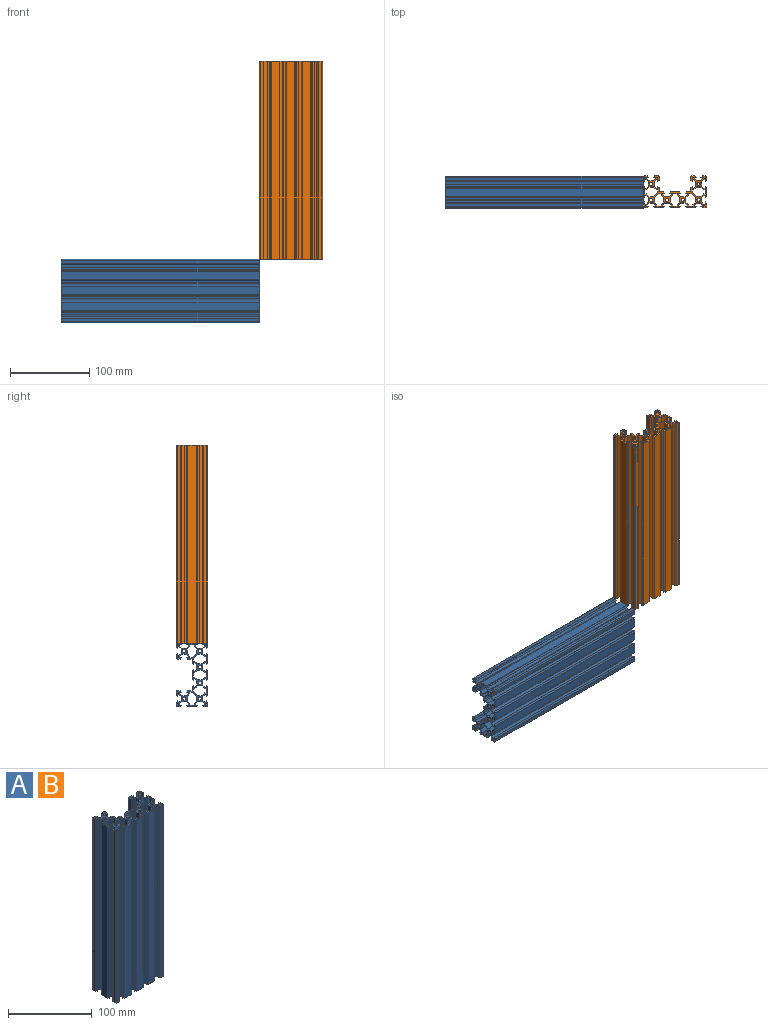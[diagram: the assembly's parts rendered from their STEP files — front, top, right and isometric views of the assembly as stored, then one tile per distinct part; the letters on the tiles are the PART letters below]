
ASSEMBLY  parts=2 mates=1
PART A: 346 faces, bbox 80x40x250 mm
  f0: cylinder r=2.1mm len=250mm, axis (0,0,-1), area 3298.7mm2, adj f6,f7
  f1: cylinder r=2.1mm len=250mm, axis (0,0,-1), area 3298.7mm2, adj f6,f7
  f2: cylinder r=2.1mm len=250mm, axis (0,0,-1), area 3298.7mm2, adj f6,f7
  f3: cylinder r=2.1mm len=250mm, axis (0,0,-1), area 3298.7mm2, adj f6,f7
  f4: cylinder r=2.1mm len=250mm, axis (0,0,-1), area 3298.7mm2, adj f6,f7
  f5: cylinder r=2.1mm len=250mm, axis (0,0,-1), area 3298.7mm2, adj f6,f7
  f6: plane 80x40mm, normal (0,0,1), area 810.2mm2, adj f0,f1,f2,f3,f4,f5,f8,f9
  f7: plane 80x40mm, normal (0,0,-1), area 810.2mm2, adj f0,f1,f2,f3,f4,f5,f8,f9
  f8: plane 250x0.11mm, normal (0.68,0.73,0), area 36.6mm2, adj f6,f7,f9,f259
  f9: plane 250x2.73mm, normal (0,1,0), area 682.1mm2, adj f6,f7,f8,f10
  f10: plane 250x2.66mm, normal (0.71,0.71,0), area 940.4mm2, adj f6,f7,f9,f11
  f11: plane 250x1.64mm, normal (1,0,0), area 410.5mm2, adj f6,f7,f10,f12
  f12: plane 250x2.61mm, normal (0,-1,0), area 653.3mm2, adj f6,f7,f11,f13
  f13: plane 250x0.11mm, normal (1,0,0), area 27.9mm2, adj f6,f7,f12,f14
  f14: plane 250x1.46mm, normal (0.71,0.71,0), area 515.7mm2, adj f6,f7,f13,f15
  f15: cylinder r=0.79mm len=250mm, axis (0,0,-1), area 155.1mm2, adj f6,f7,f14,f16
  f16: plane 250x3.6mm, normal (0,1,0), area 899mm2, adj f6,f7,f15,f17
  f17: cylinder r=1.5mm len=250mm, axis (0,0,-1), area 590.6mm2, adj f6,f7,f16,f18
  f18: plane 250x3.61mm, normal (-1,0,0), area 901.5mm2, adj f6,f7,f17,f19
  f19: cylinder r=0.79mm len=250mm, axis (0,0,-1), area 155.1mm2, adj f6,f7,f18,f20
  f20: plane 250x1.46mm, normal (-0.71,-0.71,0), area 515.7mm2, adj f6,f7,f19,f21
  f21: plane 250x0.11mm, normal (0,-1,0), area 27.5mm2, adj f6,f7,f20,f22
  f22: plane 250x2.61mm, normal (1,0,0), area 653.3mm2, adj f6,f7,f21,f23
  f23: plane 250x1.64mm, normal (0,-1,0), area 410mm2, adj f6,f7,f22,f24
  f24: plane 250x2.66mm, normal (-0.71,-0.71,0), area 940.3mm2, adj f6,f7,f23,f25
  f25: plane 250x2.74mm, normal (-1,0,0), area 684.6mm2, adj f6,f7,f24,f26
  f26: plane 250x0.1mm, normal (-0.66,-0.75,0), area 33.6mm2, adj f6,f7,f25,f27
  f27: plane 250x0.11mm, normal (-0.75,0.67,0), area 37.9mm2, adj f6,f7,f26,f28
  f28: plane 250x2.74mm, normal (-1,0,0), area 684.6mm2, adj f6,f7,f27,f29
  f29: plane 250x2.66mm, normal (-0.71,0.71,0), area 939.5mm2, adj f6,f7,f28,f30
  f30: plane 250x1.64mm, normal (0,1,0), area 410mm2, adj f6,f7,f29,f31
  f31: plane 250x2.61mm, normal (1,0,0), area 653.3mm2, adj f6,f7,f30,f32
  f32: plane 250x0.11mm, normal (0,1,0), area 27.5mm2, adj f6,f7,f31,f33
  f33: plane 250x1.46mm, normal (-0.71,0.71,0), area 514.7mm2, adj f6,f7,f32,f34
  f34: cylinder r=0.8mm len=250mm, axis (0,0,-1), area 157.1mm2, adj f6,f7,f33,f35
  f35: plane 250x10.19mm, normal (-1,0,0), area 2547.3mm2, adj f6,f7,f34,f36
  f36: cylinder r=0.8mm len=250mm, axis (0,0,-1), area 157.1mm2, adj f6,f7,f35,f37
  f37: plane 250x1.46mm, normal (-0.71,-0.71,0), area 514.7mm2, adj f6,f7,f36,f38
  f38: plane 250x0.11mm, normal (0,-1,0), area 27.5mm2, adj f6,f7,f37,f39
  f39: plane 250x2.61mm, normal (1,0,0), area 653.3mm2, adj f6,f7,f38,f40
  f40: plane 250x1.64mm, normal (0,-1,0), area 410mm2, adj f6,f7,f39,f41
  f41: plane 250x2.67mm, normal (-0.71,-0.71,0), area 941.6mm2, adj f6,f7,f40,f42
  f42: plane 250x2.74mm, normal (-1,0,0), area 684.6mm2, adj f6,f7,f41,f43
  f43: plane 250x0.09mm, normal (-0.71,-0.71,0), area 33.5mm2, adj f6,f7,f42,f44
  f44: plane 250x0.09mm, normal (-0.71,0.71,0), area 33.5mm2, adj f6,f7,f43,f45
  f45: plane 250x2.74mm, normal (-1,0,0), area 684.6mm2, adj f6,f7,f44,f46
  f46: plane 250x2.66mm, normal (-0.71,0.71,0), area 940.3mm2, adj f6,f7,f45,f47
  f47: plane 250x1.64mm, normal (0,1,0), area 410mm2, adj f6,f7,f46,f48
  f48: plane 250x2.61mm, normal (1,0,0), area 653.3mm2, adj f6,f7,f47,f49
  f49: plane 250x0.11mm, normal (0,1,0), area 27.5mm2, adj f6,f7,f48,f50
  f50: plane 250x1.46mm, normal (-0.71,0.71,0), area 515.7mm2, adj f6,f7,f49,f51
  f51: cylinder r=0.79mm len=250mm, axis (0,0,-1), area 155.1mm2, adj f6,f7,f50,f52
  f52: plane 250x3.59mm, normal (-1,0,0), area 898.2mm2, adj f6,f7,f51,f53
  f53: cylinder r=1.5mm len=250mm, axis (0,0,-1), area 589mm2, adj f6,f7,f52,f54
  f54: plane 250x3.59mm, normal (0,-1,0), area 898.2mm2, adj f6,f7,f53,f55
  f55: cylinder r=0.79mm len=250mm, axis (0,0,-1), area 158.8mm2, adj f6,f7,f54,f56
  f56: plane 250x1.46mm, normal (0.71,-0.71,0), area 515.7mm2, adj f6,f7,f55,f57
  f57: plane 250x0.11mm, normal (1,0,0), area 27.5mm2, adj f6,f7,f56,f58
  f58: plane 250x2.61mm, normal (0,1,0), area 653.3mm2, adj f6,f7,f57,f59
  f59: plane 250x1.64mm, normal (1,0,0), area 409.7mm2, adj f6,f7,f58,f60
  f60: plane 250x2.66mm, normal (0.71,-0.71,0), area 940.2mm2, adj f6,f7,f59,f61
  f61: plane 250x2.74mm, normal (0,-1,0), area 685.1mm2, adj f6,f7,f60,f62
  f62: plane 250x0.1mm, normal (0.75,-0.66,0), area 33.4mm2, adj f6,f7,f61,f63
  f63: plane 250x0.1mm, normal (-0.75,-0.66,0), area 33.4mm2, adj f6,f7,f62,f64
  f64: plane 250x2.74mm, normal (0,-1,0), area 685.1mm2, adj f6,f7,f63,f65
  f65: plane 250x2.67mm, normal (-0.71,-0.71,0), area 942.7mm2, adj f6,f7,f64,f66
  f66: plane 250x1.64mm, normal (-1,0,0), area 409.8mm2, adj f6,f7,f65,f67
  f67: plane 250x2.61mm, normal (0,1,0), area 653.3mm2, adj f6,f7,f66,f68
  f68: plane 250x0.11mm, normal (-1,0,0), area 27.5mm2, adj f6,f7,f67,f69
  f69: plane 250x1.46mm, normal (-0.71,-0.71,0), area 514.7mm2, adj f6,f7,f68,f70
  f70: cylinder r=0.8mm len=250mm, axis (0,0,-1), area 157.1mm2, adj f6,f7,f69,f71
  f71: plane 250x10.18mm, normal (0,-1,0), area 2544.3mm2, adj f6,f7,f70,f72
  f72: cylinder r=0.8mm len=250mm, axis (0,0,-1), area 157.1mm2, adj f6,f7,f71,f73
  f73: plane 250x1.46mm, normal (0.71,-0.71,0), area 514.7mm2, adj f6,f7,f72,f74
  f74: plane 250x0.11mm, normal (1,0,0), area 27.5mm2, adj f6,f7,f73,f75
  f75: plane 250x2.61mm, normal (0,1,0), area 653.3mm2, adj f6,f7,f74,f76
  f76: plane 250x1.64mm, normal (1,0,0), area 409.5mm2, adj f6,f7,f75,f77
  f77: plane 250x2.67mm, normal (0.71,-0.71,0), area 942.8mm2, adj f6,f7,f76,f78
  f78: plane 250x2.74mm, normal (0,-1,0), area 685mm2, adj f6,f7,f77,f79
  f79: plane 250x0.1mm, normal (0.71,-0.71,0), area 35.4mm2, adj f6,f7,f78,f80
  f80: plane 250x0.1mm, normal (-0.71,-0.71,0), area 35.3mm2, adj f6,f7,f79,f81
  f81: plane 250x2.74mm, normal (0,-1,0), area 684.6mm2, adj f6,f7,f80,f82
  f82: plane 250x2.67mm, normal (-0.71,-0.71,0), area 942.8mm2, adj f6,f7,f81,f83
  f83: plane 250x1.63mm, normal (-1,0.02,0), area 407.8mm2, adj f6,f7,f82,f84
  f84: plane 250x2.61mm, normal (0,1,0), area 653.3mm2, adj f6,f7,f83,f85
  f85: plane 250x0.11mm, normal (-1,0,0), area 27.5mm2, adj f6,f7,f84,f86
  f86: plane 250x1.46mm, normal (-0.71,-0.71,0), area 514.7mm2, adj f6,f7,f85,f87
  f87: cylinder r=0.8mm len=250mm, axis (0,0,-1), area 157.1mm2, adj f6,f7,f86,f88
  f88: plane 250x10.21mm, normal (0,-1,0), area 2551.6mm2, adj f6,f7,f87,f89
  f89: cylinder r=0.8mm len=250mm, axis (0,0,-1), area 157.1mm2, adj f6,f7,f88,f90
  f90: plane 250x1.46mm, normal (0.71,-0.71,0), area 514.7mm2, adj f6,f7,f89,f91
  f91: plane 250x0.11mm, normal (1,0,0), area 27.5mm2, adj f6,f7,f90,f92
  f92: plane 250x2.61mm, normal (0,1,0), area 653.3mm2, adj f6,f7,f91,f93
  f93: plane 250x1.63mm, normal (1,0.02,0), area 407.8mm2, adj f6,f7,f92,f94
  f94: plane 250x2.67mm, normal (0.71,-0.71,0), area 942.8mm2, adj f6,f7,f93,f95
  f95: plane 250x2.74mm, normal (0,-1,0), area 684.6mm2, adj f6,f7,f94,f96
  f96: plane 250x0.1mm, normal (0.71,-0.71,0), area 35.3mm2, adj f6,f7,f95,f97
  f97: plane 250x0.1mm, normal (-0.71,-0.71,0), area 35.4mm2, adj f6,f7,f96,f98
  f98: plane 250x2.74mm, normal (0,-1,0), area 685mm2, adj f6,f7,f97,f99
  f99: plane 250x2.67mm, normal (-0.71,-0.71,0), area 942.8mm2, adj f6,f7,f98,f100
  f100: plane 250x1.64mm, normal (-1,0,0), area 409.5mm2, adj f6,f7,f99,f101
  f101: plane 250x2.61mm, normal (0,1,0), area 653.3mm2, adj f6,f7,f100,f102
  f102: plane 250x0.11mm, normal (-1,0,0), area 27.5mm2, adj f6,f7,f101,f103
  f103: plane 250x1.46mm, normal (-0.71,-0.71,0), area 514.7mm2, adj f6,f7,f102,f104
  f104: cylinder r=0.8mm len=250mm, axis (0,0,-1), area 157.1mm2, adj f6,f7,f103,f105
  f105: plane 250x10.18mm, normal (0,-1,0), area 2544.3mm2, adj f6,f7,f104,f106
  f106: cylinder r=0.8mm len=250mm, axis (0,0,-1), area 157.1mm2, adj f6,f7,f105,f107
  f107: plane 250x1.46mm, normal (0.71,-0.71,0), area 514.7mm2, adj f6,f7,f106,f108
  f108: plane 250x0.11mm, normal (1,0,0), area 27.5mm2, adj f6,f7,f107,f109
  f109: plane 250x2.61mm, normal (0,1,0), area 653.3mm2, adj f6,f7,f108,f110
  f110: plane 250x1.64mm, normal (1,0,0), area 409.8mm2, adj f6,f7,f109,f111
  f111: plane 250x2.67mm, normal (0.71,-0.71,0), area 942.7mm2, adj f6,f7,f110,f112
  f112: plane 250x2.74mm, normal (0,-1,0), area 685.1mm2, adj f6,f7,f111,f113
  f113: plane 250x0.1mm, normal (0.75,-0.66,0), area 33.4mm2, adj f6,f7,f112,f114
  f114: plane 250x0.1mm, normal (-0.75,-0.66,0), area 33.4mm2, adj f6,f7,f113,f115
  f115: plane 250x2.74mm, normal (0,-1,0), area 685.1mm2, adj f6,f7,f114,f116
  f116: plane 250x2.66mm, normal (-0.71,-0.71,0), area 940.2mm2, adj f6,f7,f115,f117
  f117: plane 250x1.64mm, normal (-1,0,0), area 409.7mm2, adj f6,f7,f116,f118
  f118: plane 250x2.61mm, normal (0,1,0), area 653.3mm2, adj f6,f7,f117,f119
  f119: plane 250x0.11mm, normal (-1,0,0), area 27.5mm2, adj f6,f7,f118,f120
  f120: plane 250x1.46mm, normal (-0.71,-0.71,0), area 515.7mm2, adj f6,f7,f119,f121
  f121: cylinder r=0.79mm len=250mm, axis (0,0,-1), area 158.8mm2, adj f6,f7,f120,f122
  f122: plane 250x3.59mm, normal (0,-1,0), area 898.2mm2, adj f6,f7,f121,f123
  f123: cylinder r=1.5mm len=250mm, axis (0,0,-1), area 589mm2, adj f6,f7,f122,f124
  f124: plane 250x3.59mm, normal (1,0,0), area 898.2mm2, adj f6,f7,f123,f125
  f125: cylinder r=0.79mm len=250mm, axis (0,0,-1), area 155.1mm2, adj f6,f7,f124,f126
  f126: plane 250x1.46mm, normal (0.71,0.71,0), area 515.7mm2, adj f6,f7,f125,f127
  f127: plane 250x0.11mm, normal (0,1,0), area 27.5mm2, adj f6,f7,f126,f128
  f128: plane 250x2.61mm, normal (-1,0,0), area 653.3mm2, adj f6,f7,f127,f129
  f129: plane 250x1.64mm, normal (0,1,0), area 410mm2, adj f6,f7,f128,f130
  f130: plane 250x2.66mm, normal (0.71,0.71,0), area 940.3mm2, adj f6,f7,f129,f131
  f131: plane 250x2.74mm, normal (1,0,0), area 684.6mm2, adj f6,f7,f130,f132
  f132: plane 250x0.09mm, normal (0.71,0.71,0), area 33.5mm2, adj f6,f7,f131,f133
  f133: plane 250x0.09mm, normal (0.71,-0.71,0), area 33.5mm2, adj f6,f7,f132,f134
  f134: plane 250x2.74mm, normal (1,0,0), area 684.6mm2, adj f6,f7,f133,f135
  f135: plane 250x2.67mm, normal (0.71,-0.71,0), area 941.6mm2, adj f6,f7,f134,f136
  f136: plane 250x1.64mm, normal (0,-1,0), area 410mm2, adj f6,f7,f135,f137
  f137: plane 250x2.61mm, normal (-1,0,0), area 653.3mm2, adj f6,f7,f136,f138
  f138: plane 250x0.11mm, normal (0,-1,0), area 27.5mm2, adj f6,f7,f137,f139
  f139: plane 250x1.46mm, normal (0.71,-0.71,0), area 514.7mm2, adj f6,f7,f138,f140
  f140: cylinder r=0.8mm len=250mm, axis (0,0,-1), area 157.1mm2, adj f6,f7,f139,f141
  f141: plane 250x10.19mm, normal (1,0,0), area 2547.3mm2, adj f6,f7,f140,f142
  f142: cylinder r=0.8mm len=250mm, axis (0,0,-1), area 157.1mm2, adj f6,f7,f141,f143
  f143: plane 250x1.46mm, normal (0.71,0.71,0), area 514.7mm2, adj f6,f7,f142,f144
  f144: plane 250x0.11mm, normal (0,1,0), area 27.5mm2, adj f6,f7,f143,f145
  f145: plane 250x2.61mm, normal (-1,0,0), area 653.3mm2, adj f6,f7,f144,f146
  f146: plane 250x1.64mm, normal (0,1,0), area 410mm2, adj f6,f7,f145,f147
  f147: plane 250x2.66mm, normal (0.71,0.71,0), area 939.5mm2, adj f6,f7,f146,f148
  f148: plane 250x2.74mm, normal (1,0,0), area 684.6mm2, adj f6,f7,f147,f149
  f149: plane 250x0.11mm, normal (0.75,0.67,0), area 37.9mm2, adj f6,f7,f148,f150
  f150: plane 250x0.1mm, normal (0.66,-0.75,0), area 33.6mm2, adj f6,f7,f149,f151
  f151: plane 250x2.74mm, normal (1,0,0), area 684.6mm2, adj f6,f7,f150,f152
  f152: plane 250x2.66mm, normal (0.71,-0.71,0), area 940.3mm2, adj f6,f7,f151,f153
  f153: plane 250x1.64mm, normal (0,-1,0), area 410mm2, adj f6,f7,f152,f154
  f154: plane 250x2.61mm, normal (-1,0,0), area 653.3mm2, adj f6,f7,f153,f155
  f155: plane 250x0.11mm, normal (0,-1,0), area 27.5mm2, adj f6,f7,f154,f156
  f156: plane 250x1.46mm, normal (0.71,-0.71,0), area 515.7mm2, adj f6,f7,f155,f157
  f157: cylinder r=0.79mm len=250mm, axis (0,0,-1), area 155.1mm2, adj f6,f7,f156,f158
  f158: plane 250x3.61mm, normal (1,0,0), area 901.5mm2, adj f6,f7,f157,f159
  f159: cylinder r=1.5mm len=250mm, axis (0,0,-1), area 590.6mm2, adj f6,f7,f158,f160
  f160: plane 250x3.6mm, normal (0,1,0), area 899mm2, adj f6,f7,f159,f161
  f161: cylinder r=0.79mm len=250mm, axis (0,0,-1), area 155.1mm2, adj f6,f7,f160,f162
  f162: plane 250x1.46mm, normal (-0.71,0.71,0), area 515.7mm2, adj f6,f7,f161,f163
  f163: plane 250x0.11mm, normal (-1,0,0), area 27.9mm2, adj f6,f7,f162,f164
  f164: plane 250x2.61mm, normal (0,-1,0), area 653.3mm2, adj f6,f7,f163,f165
  f165: plane 250x1.64mm, normal (-1,0,0), area 410.5mm2, adj f6,f7,f164,f166
  f166: plane 250x2.66mm, normal (-0.71,0.71,0), area 940.4mm2, adj f6,f7,f165,f167
  f167: plane 250x2.73mm, normal (0,1,0), area 682.1mm2, adj f6,f7,f166,f168
  f168: plane 250x0.11mm, normal (-0.68,0.73,0), area 36.6mm2, adj f6,f7,f167,f169
  f169: plane 250x0.11mm, normal (0.68,0.73,0), area 36.6mm2, adj f6,f7,f168,f170
  f170: plane 250x2.73mm, normal (0,1,0), area 682.1mm2, adj f6,f7,f169,f171
  f171: plane 250x2.66mm, normal (0.71,0.71,0), area 940.4mm2, adj f6,f7,f170,f172
  f172: plane 250x1.64mm, normal (1,0,0), area 410.5mm2, adj f6,f7,f171,f173
  f173: plane 250x2.61mm, normal (0,-1,0), area 653.3mm2, adj f6,f7,f172,f174
  f174: plane 250x0.11mm, normal (1,0,0), area 27.9mm2, adj f6,f7,f173,f175
  f175: plane 250x1.46mm, normal (0.71,0.71,0), area 515.7mm2, adj f6,f7,f174,f176
  f176: cylinder r=0.79mm len=250mm, axis (0,0,-1), area 155.1mm2, adj f6,f7,f175,f177
  f177: plane 250x3.6mm, normal (0,1,0), area 899mm2, adj f6,f7,f176,f178
  f178: cylinder r=1.5mm len=250mm, axis (0,0,-1), area 590.6mm2, adj f6,f7,f177,f179
  f179: plane 250x3.61mm, normal (-1,0,0), area 901.5mm2, adj f6,f7,f178,f180
  f180: cylinder r=0.79mm len=250mm, axis (0,0,-1), area 155.1mm2, adj f6,f7,f179,f181
  f181: plane 250x1.46mm, normal (-0.71,-0.71,0), area 515.7mm2, adj f6,f7,f180,f182
  f182: plane 250x0.11mm, normal (0,-1,0), area 27.5mm2, adj f6,f7,f181,f183
  f183: plane 250x2.61mm, normal (1,0,0), area 653.3mm2, adj f6,f7,f182,f184
  f184: plane 250x1.64mm, normal (0,-1,0), area 410mm2, adj f6,f7,f183,f185
  f185: plane 250x2.66mm, normal (-0.71,-0.71,0), area 940.3mm2, adj f6,f7,f184,f186
  f186: plane 250x2.74mm, normal (-1,0,0), area 684.6mm2, adj f6,f7,f185,f187
  f187: plane 250x0.1mm, normal (-0.66,-0.75,0), area 33.6mm2, adj f6,f7,f186,f188
  f188: plane 250x0.11mm, normal (-0.75,0.67,0), area 37.9mm2, adj f6,f7,f187,f189
  f189: plane 250x2.74mm, normal (-1,0,0), area 684.6mm2, adj f6,f7,f188,f190
  f190: plane 250x2.66mm, normal (-0.71,0.71,0), area 939.5mm2, adj f6,f7,f189,f191
  f191: plane 250x1.64mm, normal (0,1,0), area 410mm2, adj f6,f7,f190,f192
  f192: plane 250x2.61mm, normal (1,0,0), area 653.3mm2, adj f6,f7,f191,f193
  f193: plane 250x0.11mm, normal (0,1,0), area 27.5mm2, adj f6,f7,f192,f194
  f194: plane 250x1.46mm, normal (-0.71,0.71,0), area 514.7mm2, adj f6,f7,f193,f195
  f195: cylinder r=0.8mm len=250mm, axis (0,0,-1), area 157.1mm2, adj f6,f7,f194,f196
  f196: plane 250x5.09mm, normal (-1,0,0), area 1271.5mm2, adj f6,f7,f195,f197
  f197: plane 250x5.1mm, normal (0,1,0), area 1275.5mm2, adj f6,f7,f196,f198
  f198: cylinder r=0.8mm len=250mm, axis (0,0,-1), area 157.6mm2, adj f6,f7,f197,f199
  f199: plane 250x1.46mm, normal (-0.71,0.71,0), area 514.7mm2, adj f6,f7,f198,f200
  f200: plane 250x0.1mm, normal (-1,0,0), area 26mm2, adj f6,f7,f199,f201
  f201: plane 250x2.61mm, normal (0,-1,0), area 653.3mm2, adj f6,f7,f200,f202
  f202: plane 250x1.64mm, normal (-1,0,0), area 410.1mm2, adj f6,f7,f201,f203
  f203: plane 250x2.66mm, normal (-0.71,0.71,0), area 940.3mm2, adj f6,f7,f202,f204
  f204: plane 250x2.74mm, normal (0,1,0), area 685mm2, adj f6,f7,f203,f205
  f205: plane 250x0.1mm, normal (-0.71,0.71,0), area 35.4mm2, adj f6,f7,f204,f206
  f206: plane 250x0.1mm, normal (0.71,0.71,0), area 35.4mm2, adj f6,f7,f205,f207
  f207: plane 250x2.74mm, normal (0,1,0), area 684.6mm2, adj f6,f7,f206,f208
  f208: plane 250x2.66mm, normal (0.71,0.71,0), area 940.3mm2, adj f6,f7,f207,f209
  f209: plane 250x1.64mm, normal (1,0,0), area 409.9mm2, adj f6,f7,f208,f210
  f210: plane 250x2.61mm, normal (0,-1,0), area 653.3mm2, adj f6,f7,f209,f211
  f211: plane 250x0.11mm, normal (1,0,0), area 27.5mm2, adj f6,f7,f210,f212
  f212: plane 250x1.46mm, normal (0.71,0.71,0), area 514.7mm2, adj f6,f7,f211,f213
  f213: cylinder r=0.8mm len=250mm, axis (0,0,-1), area 157.1mm2, adj f6,f7,f212,f214
  f214: plane 250x10.18mm, normal (0,1,0), area 2545mm2, adj f6,f7,f213,f215
  f215: cylinder r=0.8mm len=250mm, axis (0,0,-1), area 157.1mm2, adj f6,f7,f214,f216
  f216: plane 250x1.46mm, normal (-0.71,0.71,0), area 514.7mm2, adj f6,f7,f215,f217
  f217: plane 250x0.11mm, normal (-1,0,0), area 27.5mm2, adj f6,f7,f216,f218
  f218: plane 250x2.61mm, normal (0,-1,0), area 653.3mm2, adj f6,f7,f217,f219
  f219: plane 250x1.64mm, normal (-1,0,0), area 409.9mm2, adj f6,f7,f218,f220
  f220: plane 250x2.66mm, normal (-0.71,0.71,0), area 940.3mm2, adj f6,f7,f219,f221
  f221: plane 250x2.74mm, normal (0,1,0), area 684.6mm2, adj f6,f7,f220,f222
  f222: plane 250x0.1mm, normal (-0.71,0.71,0), area 35.4mm2, adj f6,f7,f221,f223
  f223: plane 250x0.1mm, normal (0.71,0.71,0), area 35.4mm2, adj f6,f7,f222,f224
  f224: plane 250x2.74mm, normal (0,1,0), area 685mm2, adj f6,f7,f223,f225
  f225: plane 250x2.66mm, normal (0.71,0.71,0), area 940.3mm2, adj f6,f7,f224,f226
  f226: plane 250x1.64mm, normal (1,0,0), area 410.1mm2, adj f6,f7,f225,f227
  f227: plane 250x2.61mm, normal (0,-1,0), area 653.3mm2, adj f6,f7,f226,f228
  f228: plane 250x0.1mm, normal (1,0,0), area 26mm2, adj f6,f7,f227,f229
  f229: plane 250x1.46mm, normal (0.71,0.71,0), area 514.7mm2, adj f6,f7,f228,f230
  f230: cylinder r=0.8mm len=250mm, axis (0,0,-1), area 157.6mm2, adj f6,f7,f229,f231
  f231: plane 250x5.1mm, normal (0,1,0), area 1275.5mm2, adj f6,f7,f230,f232
  f232: plane 250x5.09mm, normal (1,0,0), area 1271.5mm2, adj f6,f7,f231,f233
  f233: cylinder r=0.8mm len=250mm, axis (0,0,-1), area 157.1mm2, adj f6,f7,f232,f234
  f234: plane 250x1.46mm, normal (0.71,0.71,0), area 514.7mm2, adj f6,f7,f233,f235
  f235: plane 250x0.11mm, normal (0,1,0), area 27.5mm2, adj f6,f7,f234,f236
  f236: plane 250x2.61mm, normal (-1,0,0), area 653.3mm2, adj f6,f7,f235,f237
  f237: plane 250x1.64mm, normal (0,1,0), area 410mm2, adj f6,f7,f236,f238
  f238: plane 250x2.66mm, normal (0.71,0.71,0), area 939.5mm2, adj f6,f7,f237,f239
  f239: plane 250x2.74mm, normal (1,0,0), area 684.6mm2, adj f6,f7,f238,f240
  f240: plane 250x0.11mm, normal (0.75,0.67,0), area 37.9mm2, adj f6,f7,f239,f241
  f241: plane 250x0.1mm, normal (0.66,-0.75,0), area 33.6mm2, adj f6,f7,f240,f242
  f242: plane 250x2.74mm, normal (1,0,0), area 684.6mm2, adj f6,f7,f241,f243
  f243: plane 250x2.66mm, normal (0.71,-0.71,0), area 940.3mm2, adj f6,f7,f242,f244
  f244: plane 250x1.64mm, normal (0,-1,0), area 410mm2, adj f6,f7,f243,f245
  f245: plane 250x2.61mm, normal (-1,0,0), area 653.3mm2, adj f6,f7,f244,f246
  f246: plane 250x0.11mm, normal (0,-1,0), area 27.5mm2, adj f6,f7,f245,f247
  f247: plane 250x1.46mm, normal (0.71,-0.71,0), area 515.7mm2, adj f6,f7,f246,f248
  f248: cylinder r=0.79mm len=250mm, axis (0,0,-1), area 155.1mm2, adj f6,f7,f247,f249
  f249: plane 250x3.61mm, normal (1,0,0), area 901.5mm2, adj f6,f7,f248,f250
  f250: cylinder r=1.5mm len=250mm, axis (0,0,-1), area 590.6mm2, adj f6,f7,f249,f251
  f251: plane 250x3.6mm, normal (0,1,0), area 899mm2, adj f6,f7,f250,f252
  f252: cylinder r=0.79mm len=250mm, axis (0,0,-1), area 155.1mm2, adj f6,f7,f251,f253
  f253: plane 250x1.46mm, normal (-0.71,0.71,0), area 515.7mm2, adj f6,f7,f252,f254
  f254: plane 250x0.11mm, normal (-1,0,0), area 27.9mm2, adj f6,f7,f253,f255
  f255: plane 250x2.61mm, normal (0,-1,0), area 653.3mm2, adj f6,f7,f254,f256
  f256: plane 250x1.64mm, normal (-1,0,0), area 410.5mm2, adj f6,f7,f255,f257
  f257: plane 250x2.66mm, normal (-0.71,0.71,0), area 940.4mm2, adj f6,f7,f256,f258
  f258: plane 250x2.73mm, normal (0,1,0), area 682.1mm2, adj f6,f7,f257,f259
  f259: plane 250x0.11mm, normal (-0.68,0.73,0), area 36.6mm2, adj f6,f7,f8,f258
  f260: plane 250x1.63mm, normal (0,-1,0), area 407.5mm2, adj f6,f7,f261,f264
  f261: plane 250x1.63mm, normal (1,0,0), area 407.5mm2, adj f6,f7,f260,f262
  f262: plane 250x0.54mm, normal (0,1,0), area 135mm2, adj f6,f7,f261,f263
  f263: plane 250x1.09mm, normal (-0.71,0.71,0), area 385.4mm2, adj f6,f7,f262,f264
  f264: plane 250x0.54mm, normal (-1,0,0), area 135mm2, adj f6,f7,f260,f263
  f265: plane 250x5.36mm, normal (-0.71,0.71,0), area 1895mm2, adj f6,f7,f266,f275
  f266: plane 250x3.43mm, normal (-1,0,0), area 857.9mm2, adj f6,f7,f265,f267
  f267: plane 250x1.96mm, normal (0,-1,0), area 490.5mm2, adj f6,f7,f266,f268
  f268: plane 250x3.4mm, normal (-0.71,-0.71,0), area 1202mm2, adj f6,f7,f267,f269
  f269: plane 250x5.67mm, normal (0,-1,0), area 1417.5mm2, adj f6,f7,f268,f270
  f270: plane 250x3.4mm, normal (0.71,-0.71,0), area 1202mm2, adj f6,f7,f269,f271
  f271: plane 250x1.96mm, normal (0,-1,0), area 490.5mm2, adj f6,f7,f270,f272
  f272: plane 250x5.39mm, normal (1,0,0), area 1348mm2, adj f6,f7,f271,f273
  f273: plane 250x1.96mm, normal (0,1,0), area 490mm2, adj f6,f7,f272,f274
  f274: plane 250x3.4mm, normal (0.71,0.71,0), area 1202mm2, adj f6,f7,f273,f275
  f275: plane 250x5.68mm, normal (0,1,0), area 1420.1mm2, adj f6,f7,f265,f274
  f276: plane 250x5.37mm, normal (0.71,-0.71,0), area 1898.5mm2, adj f6,f7,f277,f286
  f277: plane 250x5.67mm, normal (1,0,0), area 1416.5mm2, adj f6,f7,f276,f278
  f278: plane 250x3.41mm, normal (0.71,0.71,0), area 1205.3mm2, adj f6,f7,f277,f279
  f279: plane 250x1.95mm, normal (1,0,0), area 486.8mm2, adj f6,f7,f278,f280
  f280: plane 250x5.39mm, normal (0,1,0), area 1347.6mm2, adj f6,f7,f279,f281
  f281: plane 250x1.95mm, normal (-1,0,0), area 487.5mm2, adj f6,f7,f280,f282
  f282: plane 250x3.41mm, normal (-0.71,0.71,0), area 1205.5mm2, adj f6,f7,f281,f283
  f283: plane 250x5.67mm, normal (-1,0,0), area 1417.7mm2, adj f6,f7,f282,f284
  f284: plane 250x3.41mm, normal (-0.71,-0.71,0), area 1205.5mm2, adj f6,f7,f283,f285
  f285: plane 250x1.95mm, normal (-1,0,0), area 487.9mm2, adj f6,f7,f284,f286
  f286: plane 250x3.43mm, normal (0,-1,0), area 857.6mm2, adj f6,f7,f276,f285
  f287: plane 250x0.54mm, normal (-1,0,0), area 135mm2, adj f6,f7,f288,f291
  f288: plane 250x1.09mm, normal (-0.71,-0.71,0), area 385.4mm2, adj f6,f7,f287,f289
  f289: plane 250x0.54mm, normal (0,-1,0), area 135mm2, adj f6,f7,f288,f290
  f290: plane 250x1.63mm, normal (1,0,0), area 407.5mm2, adj f6,f7,f289,f291
  f291: plane 250x1.63mm, normal (0,1,0), area 407.5mm2, adj f6,f7,f287,f290
  f292: plane 250x1.96mm, normal (1,0,0), area 490mm2, adj f6,f7,f293,f303
  f293: plane 250x5.36mm, normal (0,1,0), area 1340.4mm2, adj f6,f7,f292,f294
  f294: plane 250x1.96mm, normal (-1,0,0), area 490mm2, adj f6,f7,f293,f295
  f295: plane 250x3.41mm, normal (-0.71,0.71,0), area 1205.5mm2, adj f6,f7,f294,f296
  f296: plane 250x5.66mm, normal (-1,0,0), area 1415.2mm2, adj f6,f7,f295,f297
  f297: plane 250x3.41mm, normal (-0.71,-0.71,0), area 1205.5mm2, adj f6,f7,f296,f298
  f298: plane 250x1.96mm, normal (-1,0,0), area 490mm2, adj f6,f7,f297,f299
  f299: plane 250x5.36mm, normal (0,-1,0), area 1340.4mm2, adj f6,f7,f298,f300
  f300: plane 250x1.96mm, normal (1,0,0), area 490mm2, adj f6,f7,f299,f301
  f301: plane 250x3.41mm, normal (0.71,-0.71,0), area 1205.5mm2, adj f6,f7,f300,f302
  f302: plane 250x5.66mm, normal (1,0,0), area 1415.2mm2, adj f6,f7,f301,f303
  f303: plane 250x3.41mm, normal (0.71,0.71,0), area 1205.5mm2, adj f6,f7,f292,f302
  f304: plane 250x1.63mm, normal (0,-1,0), area 407.5mm2, adj f6,f7,f305,f308
  f305: plane 250x1.63mm, normal (1,0,0), area 407.5mm2, adj f6,f7,f304,f306
  f306: plane 250x0.54mm, normal (0,1,0), area 135mm2, adj f6,f7,f305,f307
  f307: plane 250x1.09mm, normal (-0.71,0.71,0), area 385.4mm2, adj f6,f7,f306,f308
  f308: plane 250x0.54mm, normal (-1,0,0), area 135mm2, adj f6,f7,f304,f307
  f309: plane 250x3.43mm, normal (1,0,0), area 857.9mm2, adj f6,f7,f310,f319
  f310: plane 250x5.36mm, normal (0.71,0.71,0), area 1895mm2, adj f6,f7,f309,f311
  f311: plane 250x5.68mm, normal (0,1,0), area 1420.1mm2, adj f6,f7,f310,f312
  f312: plane 250x3.4mm, normal (-0.71,0.71,0), area 1202mm2, adj f6,f7,f311,f313
  f313: plane 250x1.96mm, normal (0,1,0), area 490mm2, adj f6,f7,f312,f314
  f314: plane 250x5.39mm, normal (-1,0,0), area 1348mm2, adj f6,f7,f313,f315
  f315: plane 250x1.96mm, normal (0,-1,0), area 490.5mm2, adj f6,f7,f314,f316
  f316: plane 250x3.4mm, normal (-0.71,-0.71,0), area 1202mm2, adj f6,f7,f315,f317
  f317: plane 250x5.67mm, normal (0,-1,0), area 1417.5mm2, adj f6,f7,f316,f318
  f318: plane 250x3.4mm, normal (0.71,-0.71,0), area 1202mm2, adj f6,f7,f317,f319
  f319: plane 250x1.96mm, normal (0,-1,0), area 490.5mm2, adj f6,f7,f309,f318
  f320: plane 250x5.67mm, normal (-1,0,0), area 1416.5mm2, adj f6,f7,f321,f330
  f321: plane 250x5.37mm, normal (-0.71,-0.71,0), area 1898.5mm2, adj f6,f7,f320,f322
  f322: plane 250x3.43mm, normal (0,-1,0), area 857.6mm2, adj f6,f7,f321,f323
  f323: plane 250x1.95mm, normal (1,0,0), area 487.9mm2, adj f6,f7,f322,f324
  f324: plane 250x3.41mm, normal (0.71,-0.71,0), area 1205.5mm2, adj f6,f7,f323,f325
  f325: plane 250x5.67mm, normal (1,0,0), area 1417.7mm2, adj f6,f7,f324,f326
  f326: plane 250x3.41mm, normal (0.71,0.71,0), area 1205.5mm2, adj f6,f7,f325,f327
  f327: plane 250x1.95mm, normal (1,0,0), area 487.5mm2, adj f6,f7,f326,f328
  f328: plane 250x5.39mm, normal (0,1,0), area 1347.6mm2, adj f6,f7,f327,f329
  f329: plane 250x1.95mm, normal (-1,0,0), area 486.8mm2, adj f6,f7,f328,f330
  f330: plane 250x3.41mm, normal (-0.71,0.71,0), area 1205.3mm2, adj f6,f7,f320,f329
  f331: plane 250x1.63mm, normal (0,1,0), area 407.5mm2, adj f6,f7,f332,f335
  f332: plane 250x1.63mm, normal (-1,0,0), area 407.5mm2, adj f6,f7,f331,f333
  f333: plane 250x0.54mm, normal (0,-1,0), area 135mm2, adj f6,f7,f332,f334
  f334: plane 250x1.09mm, normal (0.71,-0.71,0), area 385.4mm2, adj f6,f7,f333,f335
  f335: plane 250x0.54mm, normal (1,0,0), area 135mm2, adj f6,f7,f331,f334
  f336: plane 250x0.54mm, normal (1,0,0), area 135mm2, adj f6,f7,f337,f340
  f337: plane 250x1.09mm, normal (0.71,0.71,0), area 385.4mm2, adj f6,f7,f336,f338
  f338: plane 250x0.54mm, normal (0,1,0), area 135mm2, adj f6,f7,f337,f339
  f339: plane 250x1.63mm, normal (-1,0,0), area 407.5mm2, adj f6,f7,f338,f340
  f340: plane 250x1.63mm, normal (0,-1,0), area 407.5mm2, adj f6,f7,f336,f339
  f341: plane 250x0.54mm, normal (1,0,0), area 135mm2, adj f6,f7,f342,f345
  f342: plane 250x1.09mm, normal (0.71,0.71,0), area 385.4mm2, adj f6,f7,f341,f343
  f343: plane 250x0.54mm, normal (0,1,0), area 135mm2, adj f6,f7,f342,f344
  f344: plane 250x1.63mm, normal (-1,0,0), area 407.5mm2, adj f6,f7,f343,f345
  f345: plane 250x1.63mm, normal (0,-1,0), area 407.5mm2, adj f6,f7,f341,f344
PART B: same geometry as A
PLACE A rot(axis=(0,1,0),90deg) t=(-276.65,-4.64,35.42)mm
PLACE B t=(-16.65,-4.64,45.42)mm
MATE fastened B.f35 <-> A.f6  axis (-1,0,0) through (-26.65,-14.64,45.42)mm
